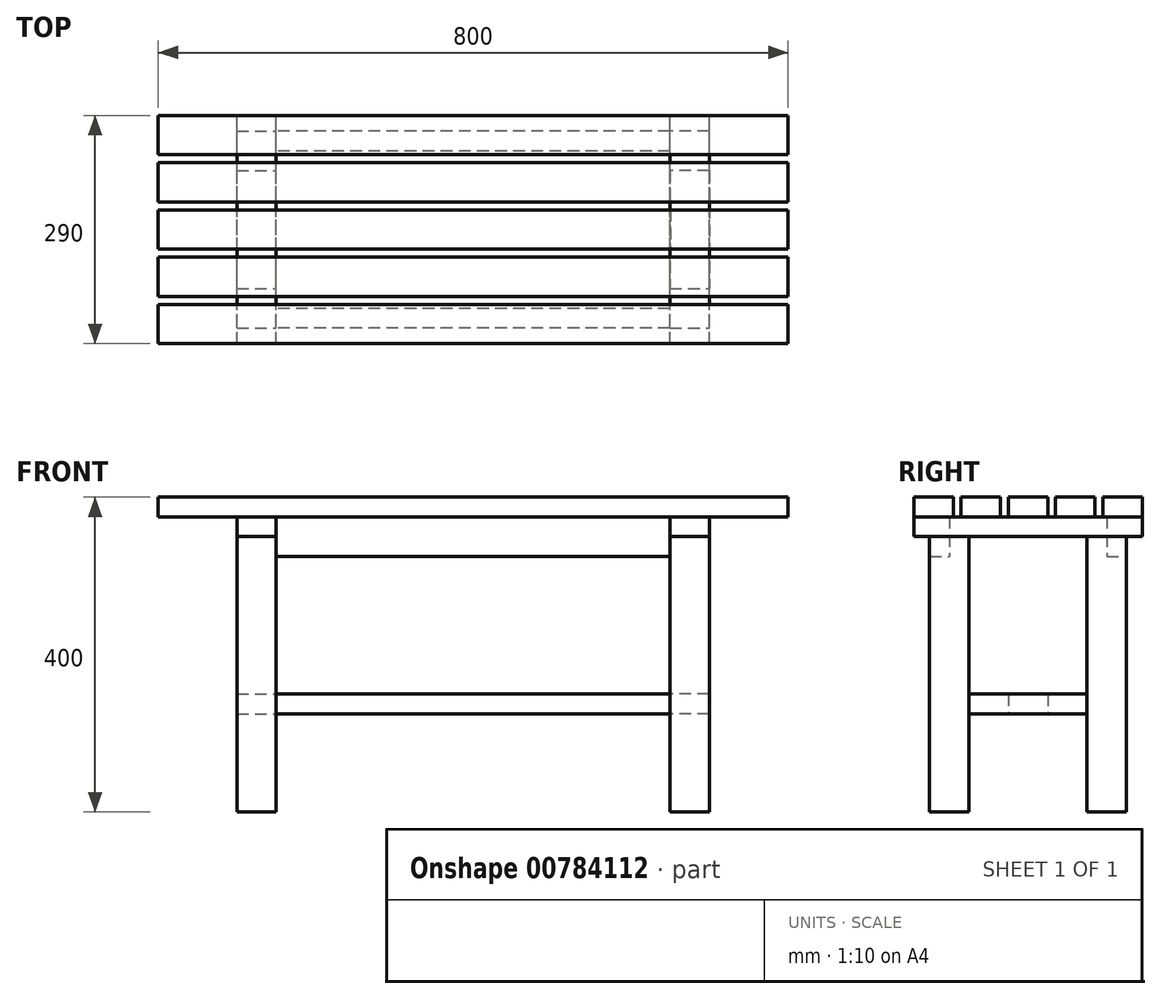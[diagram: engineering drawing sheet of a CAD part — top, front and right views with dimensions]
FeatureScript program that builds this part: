
annotation { "Feature Type Name" : "Feature", "Feature Type Description" : "" }
export const myFeature = defineFeature(function(context is Context, id is Id, definition is map)
    precondition{}
    {
        {
            var Q0;
            Q0=qCreatedBy(makeId("Top.planeOp"),FACE);
            var sketch = newSketch(context, id + "F0", { "sketchPlane" : qUnion([Q0])});
            skLineSegment(sketch, "E0.bottom", {"start": v(0, 0) * mm, "end": v(800, 0) * mm});
            skLineSegment(sketch, "E0.top", {"start": v(0, 290) * mm, "end": v(800, 290) * mm});
            skLineSegment(sketch, "E0.left", {"start": v(0, 0) * mm, "end": v(0, 290) * mm});
            skLineSegment(sketch, "E0.right", {"start": v(800, 0) * mm, "end": v(800, 290) * mm});
            skLineSegment(sketch, "E1.top", {"start": v(0, 240) * mm, "end": v(800, 240) * mm});
            skLineSegment(sketch, "E1.left", {"start": v(0, 290) * mm, "end": v(0, 240) * mm});
            skLineSegment(sketch, "E1.right", {"start": v(800, 290) * mm, "end": v(800, 240) * mm});
            skLineSegment(sketch, "E2.bottom", {"start": v(0, 230) * mm, "end": v(800, 230) * mm});
            skLineSegment(sketch, "E2.top", {"start": v(0, 110) * mm, "end": v(800, 110) * mm});
            skLineSegment(sketch, "E2.left", {"start": v(0, 230) * mm, "end": v(0, 110) * mm});
            skLineSegment(sketch, "E2.right", {"start": v(800, 230) * mm, "end": v(800, 110) * mm});
            skLineSegment(sketch, "E3.top", {"start": v(0, 50) * mm, "end": v(800, 50) * mm});
            skLineSegment(sketch, "E3.left", {"start": v(0, 0) * mm, "end": v(0, 50) * mm});
            skLineSegment(sketch, "E3.right", {"start": v(800, 0) * mm, "end": v(800, 50) * mm});
            skLineSegment(sketch, "E4.top", {"start": v(0, 180) * mm, "end": v(800, 180) * mm});
            skLineSegment(sketch, "E4.left", {"start": v(0, 230) * mm, "end": v(0, 180) * mm});
            skLineSegment(sketch, "E4.right", {"start": v(800, 230) * mm, "end": v(800, 180) * mm});
            skLineSegment(sketch, "E5.bottom", {"start": v(0, 170) * mm, "end": v(800, 170) * mm});
            skLineSegment(sketch, "E5.top", {"start": v(0, 120) * mm, "end": v(800, 120) * mm});
            skLineSegment(sketch, "E5.left", {"start": v(0, 170) * mm, "end": v(0, 120) * mm});
            skLineSegment(sketch, "E5.right", {"start": v(800, 170) * mm, "end": v(800, 120) * mm});
            skLineSegment(sketch, "E6.top", {"start": v(0, 60) * mm, "end": v(800, 60) * mm});
            skLineSegment(sketch, "E6.left", {"start": v(0, 110) * mm, "end": v(0, 60) * mm});
            skLineSegment(sketch, "E6.right", {"start": v(800, 110) * mm, "end": v(800, 60) * mm});
            skLineSegment(sketch, "E7.left", {"start": v(0, 50) * mm, "end": v(0, 0) * mm});
            skLineSegment(sketch, "E7.right", {"start": v(800, 50) * mm, "end": v(800, 0) * mm});
            skSolve(sketch);
        }
        {
            var Q0;
            Q0=makeQuery(id+"F0.imprint","IMPRINT",FACE,{"disambiguationData":[TD([[makeQuery(id+"F0.imprint","IMPRINT",EDGE,{"derivedFrom":sQuery(id+"F0.wireOp",EDGE,"E0.top")}),-1.0]])]});
            var Q1;
            Q1=makeQuery(id+"F0.imprint","IMPRINT",FACE,{"disambiguationData":[TD([[makeQuery(id+"F0.imprint","IMPRINT",EDGE,{"derivedFrom":sQuery(id+"F0.wireOp",EDGE,"E2.bottom")}),-1.0]])]});
            var Q2;
            Q2=makeQuery(id+"F0.imprint","IMPRINT",FACE,{"disambiguationData":[TD([[makeQuery(id+"F0.imprint","IMPRINT",EDGE,{"derivedFrom":sQuery(id+"F0.wireOp",EDGE,"E5.bottom")}),-1.0]])]});
            var Q3;
            Q3=makeQuery(id+"F0.imprint","IMPRINT",FACE,{"disambiguationData":[TD([[makeQuery(id+"F0.imprint","IMPRINT",EDGE,{"derivedFrom":sQuery(id+"F0.wireOp",EDGE,"E2.top")}),-1.0]])]});
            var Q4;
            Q4=makeQuery(id+"F0.imprint","IMPRINT",FACE,{"disambiguationData":[TD([[makeQuery(id+"F0.imprint","IMPRINT",EDGE,{"derivedFrom":sQuery(id+"F0.wireOp",EDGE,"E3.top")}),-1.0]])]});
            extrude(context, id + "F1", {"entities" : qUnion([Q0, Q1, Q2, Q3, Q4]), "depth" : 25 * mm, "offsetDistance" : 25 * mm});
        }
        {
            var Q0;
            Q0=makeQuery(id+"F1.opExtrude","CAP_FACE",FACE,{"disambiguationData":[OSD([sQuery(id+"F0.wireOp",EDGE,"E3.top"),sQuery(id+"F0.wireOp",EDGE,"E0.bottom"),sQuery(id+"F0.wireOp",EDGE,"E7.left"),sQuery(id+"F0.wireOp",EDGE,"E7.right")])],"isStart":true});
            var sketch = newSketch(context, id + "F2", { "sketchPlane" : qUnion([Q0])});
            skLineSegment(sketch, "E8.bottom", {"start": v(100, 0) * mm, "end": v(150, 0) * mm});
            skLineSegment(sketch, "E8.top", {"start": v(100, -290) * mm, "end": v(150, -290) * mm});
            skLineSegment(sketch, "E8.left", {"start": v(100, 0) * mm, "end": v(100, -290) * mm});
            skLineSegment(sketch, "E8.right", {"start": v(150, 0) * mm, "end": v(150, -290) * mm});
            skLineSegment(sketch, "E9.bottom", {"start": v(650, 0) * mm, "end": v(700, 0) * mm});
            skLineSegment(sketch, "E9.top", {"start": v(650, -290) * mm, "end": v(700, -290) * mm});
            skLineSegment(sketch, "E9.left", {"start": v(650, 0) * mm, "end": v(650, -290) * mm});
            skLineSegment(sketch, "E9.right", {"start": v(700, 0) * mm, "end": v(700, -290) * mm});
            skSolve(sketch);
        }
        {
            var Q0;
            {var subQ0=sQuery(id+"F2.wireOp",EDGE,"E8.top");Q0=makeQuery(id+"F2.imprint","IMPRINT",FACE,{"disambiguationData":[TD([[makeQuery(id+"F2.imprint","IMPRINT",EDGE,{"derivedFrom":subQ0}),1.0]])]});}
            var Q1;
            {var subQ0=sQuery(id+"F2.wireOp",EDGE,"E8.bottom");Q1=makeQuery(id+"F2.imprint","IMPRINT",FACE,{"disambiguationData":[TD([[makeQuery(id+"F2.imprint","IMPRINT",EDGE,{"derivedFrom":subQ0}),-1.0]])]});}
            var Q2;
            {var subQ0=sQuery(id+"F2.wireOp",EDGE,"E9.bottom");Q2=makeQuery(id+"F2.imprint","IMPRINT",FACE,{"disambiguationData":[TD([[makeQuery(id+"F2.imprint","IMPRINT",EDGE,{"derivedFrom":subQ0}),-1.0]])]});}
            var Q3;
            {var subQ0=sQuery(id+"F2.wireOp",EDGE,"E9.top");Q3=makeQuery(id+"F2.imprint","IMPRINT",FACE,{"disambiguationData":[TD([[makeQuery(id+"F2.imprint","IMPRINT",EDGE,{"derivedFrom":subQ0}),1.0]])]});}
            extrude(context, id + "F3", {"entities" : qUnion([Q0, Q1, Q2, Q3]), "depth" : 25 * mm, "offsetDistance" : 25 * mm});
        }
        {
            var Q0;
            Q0=makeQuery(id+"F3.opExtrude","CAP_FACE",FACE,{"disambiguationData":[OSD([sQuery(id+"F2.wireOp",EDGE,"E8.bottom"),sQuery(id+"F2.wireOp",EDGE,"E8.top"),sQuery(id+"F2.wireOp",EDGE,"E8.left"),sQuery(id+"F2.wireOp",EDGE,"E8.right")])],"isStart":false});
            var sketch = newSketch(context, id + "F4", { "sketchPlane" : qUnion([Q0])});
            skLineSegment(sketch, "E10.bottom", {"start": v(100, -270) * mm, "end": v(150, -270) * mm});
            skLineSegment(sketch, "E10.top", {"start": v(100, -220) * mm, "end": v(150, -220) * mm});
            skLineSegment(sketch, "E10.left", {"start": v(100, -270) * mm, "end": v(100, -220) * mm});
            skLineSegment(sketch, "E10.right", {"start": v(150, -270) * mm, "end": v(150, -220) * mm});
            skLineSegment(sketch, "E11.top", {"start": v(100, -20) * mm, "end": v(150, -20) * mm});
            skLineSegment(sketch, "E12.top", {"start": v(100, -70) * mm, "end": v(150, -70) * mm});
            skLineSegment(sketch, "E12.left", {"start": v(100, -20) * mm, "end": v(100, -70) * mm});
            skLineSegment(sketch, "E12.right", {"start": v(150, -20) * mm, "end": v(150, -70) * mm});
            skSolve(sketch);
        }
        {
            var Q0;
            Q0=makeQuery(id+"F4.imprint","IMPRINT",FACE,{"disambiguationData":[TD([[makeQuery(id+"F4.imprint","IMPRINT",EDGE,{"derivedFrom":sQuery(id+"F4.wireOp",EDGE,"E10.bottom")}),1.0]])]});
            var Q1;
            Q1=makeQuery(id+"F4.imprint","IMPRINT",FACE,{"disambiguationData":[TD([[makeQuery(id+"F4.imprint","IMPRINT",EDGE,{"derivedFrom":sQuery(id+"F4.wireOp",EDGE,"E11.top")}),-1.0]])]});
            extrude(context, id + "F5", {"entities" : qUnion([Q0, Q1]), "depth" : 350 * mm, "offsetDistance" : 25 * mm});
        }
        {
            var Q0;
            Q0=makeQuery(id+"F3.opExtrude","CAP_FACE",FACE,{"disambiguationData":[OSD([sQuery(id+"F2.wireOp",EDGE,"E9.bottom"),sQuery(id+"F2.wireOp",EDGE,"E9.top"),sQuery(id+"F2.wireOp",EDGE,"E9.left"),sQuery(id+"F2.wireOp",EDGE,"E9.right")])],"isStart":false});
            var sketch = newSketch(context, id + "F6", { "sketchPlane" : qUnion([Q0])});
            skLineSegment(sketch, "E13.bottom", {"start": v(700, -270) * mm, "end": v(650, -270) * mm});
            skLineSegment(sketch, "E13.top", {"start": v(700, -220) * mm, "end": v(650, -220) * mm});
            skLineSegment(sketch, "E13.left", {"start": v(700, -270) * mm, "end": v(700, -220) * mm});
            skLineSegment(sketch, "E13.right", {"start": v(650, -270) * mm, "end": v(650, -220) * mm});
            skLineSegment(sketch, "E14.bottom", {"start": v(650, -20) * mm, "end": v(700, -20) * mm});
            skLineSegment(sketch, "E14.top", {"start": v(650, -70) * mm, "end": v(700, -70) * mm});
            skLineSegment(sketch, "E14.left", {"start": v(650, -20) * mm, "end": v(650, -70) * mm});
            skLineSegment(sketch, "E14.right", {"start": v(700, -20) * mm, "end": v(700, -70) * mm});
            skSolve(sketch);
        }
        {
            var Q0;
            Q0=makeQuery(id+"F6.imprint","IMPRINT",FACE,{"disambiguationData":[TD([[makeQuery(id+"F6.imprint","IMPRINT",EDGE,{"derivedFrom":sQuery(id+"F6.wireOp",EDGE,"E14.bottom")}),-1.0]])]});
            var Q1;
            Q1=makeQuery(id+"F6.imprint","IMPRINT",FACE,{"disambiguationData":[TD([[makeQuery(id+"F6.imprint","IMPRINT",EDGE,{"derivedFrom":sQuery(id+"F6.wireOp",EDGE,"E13.bottom")}),-1.0]])]});
            extrude(context, id + "F7", {"entities" : qUnion([Q0, Q1]), "depth" : 350 * mm, "offsetDistance" : 25 * mm});
        }
        {
            var Q0;
            Q0=makeQuery(id+"F7.opExtrude","CAP_FACE",FACE,{"disambiguationData":[OSD([sQuery(id+"F6.wireOp",EDGE,"E13.bottom"),sQuery(id+"F6.wireOp",EDGE,"E13.top"),sQuery(id+"F6.wireOp",EDGE,"E13.left"),sQuery(id+"F6.wireOp",EDGE,"E13.right")])],"isStart":false});
            var sketch = newSketch(context, id + "F8", { "sketchPlane" : qUnion([Q0])});
            skLineSegment(sketch, "E15.bottom", {"start": v(700, -220) * mm, "end": v(650, -220) * mm});
            skLineSegment(sketch, "E15.top", {"start": v(700, -70) * mm, "end": v(650, -70) * mm});
            skLineSegment(sketch, "E15.left", {"start": v(700, -220) * mm, "end": v(700, -70) * mm});
            skLineSegment(sketch, "E15.right", {"start": v(650, -220) * mm, "end": v(650, -70) * mm});
            skSolve(sketch);
        }
        {
            var Q0;
            Q0=makeQuery(id+"F8.imprint","IMPRINT",FACE,{"disambiguationData":[TD([[makeQuery(id+"F8.imprint","IMPRINT",EDGE,{"derivedFrom":sQuery(id+"F8.wireOp",EDGE,"E15.bottom")}),-1.0]])]});
            extrude(context, id + "F9", {"entities" : qUnion([Q0]), "depth" : 25 * mm, "offsetDistance" : 25 * mm});
        }
        {
            var Q0;
            Q0=makeQuery(id+"F5.opExtrude","CAP_FACE",FACE,{"disambiguationData":[OSD([sQuery(id+"F4.wireOp",EDGE,"E11.top"),sQuery(id+"F4.wireOp",EDGE,"E12.top"),sQuery(id+"F4.wireOp",EDGE,"E12.left"),sQuery(id+"F4.wireOp",EDGE,"E12.right")])],"isStart":false});
            var sketch = newSketch(context, id + "F10", { "sketchPlane" : qUnion([Q0])});
            skLineSegment(sketch, "E16.bottom", {"start": v(100, -70) * mm, "end": v(150, -70) * mm});
            skLineSegment(sketch, "E16.top", {"start": v(100, -220) * mm, "end": v(150, -220) * mm});
            skLineSegment(sketch, "E16.left", {"start": v(100, -70) * mm, "end": v(100, -220) * mm});
            skLineSegment(sketch, "E16.right", {"start": v(150, -70) * mm, "end": v(150, -220) * mm});
            skSolve(sketch);
        }
        {
            var Q0;
            Q0=makeQuery(id+"F10.imprint","IMPRINT",FACE,{"disambiguationData":[TD([[makeQuery(id+"F10.imprint","IMPRINT",EDGE,{"derivedFrom":sQuery(id+"F10.wireOp",EDGE,"E16.bottom")}),-1.0]])]});
            extrude(context, id + "F11", {"entities" : qUnion([Q0]), "depth" : 25 * mm, "offsetDistance" : 25 * mm});
        }
        {
            var Q0;
            Q0=makeQuery(id+"F11.opExtrude","CAP_FACE",FACE,{"disambiguationData":[OSD([sQuery(id+"F10.wireOp",EDGE,"E16.bottom"),sQuery(id+"F10.wireOp",EDGE,"E16.top"),sQuery(id+"F10.wireOp",EDGE,"E16.left"),sQuery(id+"F10.wireOp",EDGE,"E16.right")])],"isStart":false});
            var sketch = newSketch(context, id + "F12", { "sketchPlane" : qUnion([Q0])});
            skLineSegment(sketch, "E17.bottom", {"start": v(150, -145) * mm, "end": v(650.72, -145) * mm});
            skLineSegment(sketch, "E17.top", {"start": v(150, -170) * mm, "end": v(650.72, -170) * mm});
            skLineSegment(sketch, "E17.left", {"start": v(150, -145) * mm, "end": v(150, -170) * mm});
            skLineSegment(sketch, "E17.right", {"start": v(650.72, -145) * mm, "end": v(650.72, -170) * mm});
            skLineSegment(sketch, "E18.MirrorCS", {"start": v(150, -120) * mm, "end": v(650.72, -120) * mm});
            skLineSegment(sketch, "E19.MirrorCS", {"start": v(150, -145) * mm, "end": v(150, -120) * mm});
            skLineSegment(sketch, "E20.MirrorCS", {"start": v(650.72, -145) * mm, "end": v(650.72, -120) * mm});
            skSolve(sketch);
        }
        {
            var Q0;
            Q0=makeQuery(id+"F12.imprint","IMPRINT",FACE,{"disambiguationData":[TD([[makeQuery(id+"F12.imprint","IMPRINT",EDGE,{"derivedFrom":sQuery(id+"F12.wireOp",EDGE,"E17.bottom")}),1.0]])]});
            var Q1;
            Q1=makeQuery(id+"F12.imprint","IMPRINT",FACE,{"disambiguationData":[TD([[makeQuery(id+"F12.imprint","IMPRINT",EDGE,{"derivedFrom":sQuery(id+"F12.wireOp",EDGE,"E17.bottom")}),-1.0]])]});
            extrude(context, id + "F13", {"entities" : qUnion([Q0, Q1]), "depth" : -25 * mm, "offsetDistance" : 25 * mm});
        }
        {
            var Q0;
            Q0=makeQuery(id+"F11.opExtrude","SWEPT_BODY",BODY,{"disambiguationData":[OSD([sQuery(id+"F10.wireOp",EDGE,"E16.bottom"),sQuery(id+"F10.wireOp",EDGE,"E16.top"),sQuery(id+"F10.wireOp",EDGE,"E16.left"),sQuery(id+"F10.wireOp",EDGE,"E16.right")])]});
            var Q1;
            Q1=makeQuery(id+"F13.opExtrude","SWEPT_BODY",BODY,{"disambiguationData":[OSD([sQuery(id+"F12.wireOp",EDGE,"E17.top"),sQuery(id+"F12.wireOp",EDGE,"E17.left"),sQuery(id+"F12.wireOp",EDGE,"E17.right"),sQuery(id+"F12.wireOp",EDGE,"E18.MirrorCS"),sQuery(id+"F12.wireOp",EDGE,"E19.MirrorCS"),sQuery(id+"F12.wireOp",EDGE,"E20.MirrorCS")])]});
            var Q2;
            Q2=makeQuery(id+"F9.opExtrude","SWEPT_BODY",BODY,{"disambiguationData":[OSD([sQuery(id+"F8.wireOp",EDGE,"E15.bottom"),sQuery(id+"F8.wireOp",EDGE,"E15.top"),sQuery(id+"F8.wireOp",EDGE,"E15.left"),sQuery(id+"F8.wireOp",EDGE,"E15.right")])]});
            var Q3;
            Q3=makeQuery(id+"F13.opExtrude","CAP_FACE",FACE,{"disambiguationData":[OSD([sQuery(id+"F12.wireOp",EDGE,"E17.top"),sQuery(id+"F12.wireOp",EDGE,"E17.left"),sQuery(id+"F12.wireOp",EDGE,"E17.right"),sQuery(id+"F12.wireOp",EDGE,"E18.MirrorCS"),sQuery(id+"F12.wireOp",EDGE,"E19.MirrorCS"),sQuery(id+"F12.wireOp",EDGE,"E20.MirrorCS")])],"isStart":false});
            transform(context, id + "F14", {"entities" : qUnion([Q0, Q1, Q2]), "transformType" : TransformType.TRANSLATION_DISTANCE, "transformDirection" : qUnion([Q3]), "distance" : 150 * mm, "makeCopy" : false});
        }
        {
            var Q0;
            Q0=makeQuery(id+"F3.opExtrude","SWEPT_FACE",FACE,{"disambiguationData":[OSD([sQuery(id+"F2.wireOp",EDGE,"E8.right")])]});
            var sketch = newSketch(context, id + "F15", { "sketchPlane" : qUnion([Q0])});
            skLineSegment(sketch, "E21.bottom", {"start": v(20, 0) * mm, "end": v(45, 0) * mm});
            skLineSegment(sketch, "E21.top", {"start": v(20, -50) * mm, "end": v(45, -50) * mm});
            skLineSegment(sketch, "E21.left", {"start": v(20, 0) * mm, "end": v(20, -50) * mm});
            skLineSegment(sketch, "E21.right", {"start": v(45, 0) * mm, "end": v(45, -50) * mm});
            skSolve(sketch);
        }
        {
            var Q0;
            {var subQ0=sQuery(id+"F15.wireOp",EDGE,"E21.top");Q0=makeQuery(id+"F15.imprint","IMPRINT",FACE,{"disambiguationData":[TD([[makeQuery(id+"F15.imprint","IMPRINT",EDGE,{"derivedFrom":subQ0}),1.0]])]});}
            var Q1;
            {var subQ0=sQuery(id+"F15.wireOp",EDGE,"E21.bottom");Q1=makeQuery(id+"F15.imprint","IMPRINT",FACE,{"disambiguationData":[TD([[makeQuery(id+"F15.imprint","IMPRINT",EDGE,{"derivedFrom":subQ0}),-1.0]])]});}
            extrude(context, id + "F16", {"entities" : qUnion([Q0, Q1]), "depth" : 500 * mm, "offsetDistance" : 25 * mm});
        }
        {
            var Q0;
            Q0=makeQuery(id+"F16.opExtrude","SWEPT_BODY",BODY,{"disambiguationData":[OSD([sQuery(id+"F15.wireOp",EDGE,"E21.bottom"),sQuery(id+"F15.wireOp",EDGE,"E21.top"),sQuery(id+"F15.wireOp",EDGE,"E21.left"),sQuery(id+"F15.wireOp",EDGE,"E21.right")])]});
            var Q1;
            Q1=makeQuery(id+"F16.opExtrude","SWEPT_FACE",FACE,{"disambiguationData":[OSD([sQuery(id+"F15.wireOp",EDGE,"E21.right")])]});
            transform(context, id + "F17", {"entities" : qUnion([Q0]), "transformType" : TransformType.TRANSLATION_DISTANCE, "transformDirection" : qUnion([Q1]), "distance" : 225 * mm, "makeCopy" : true});
        }
    });
